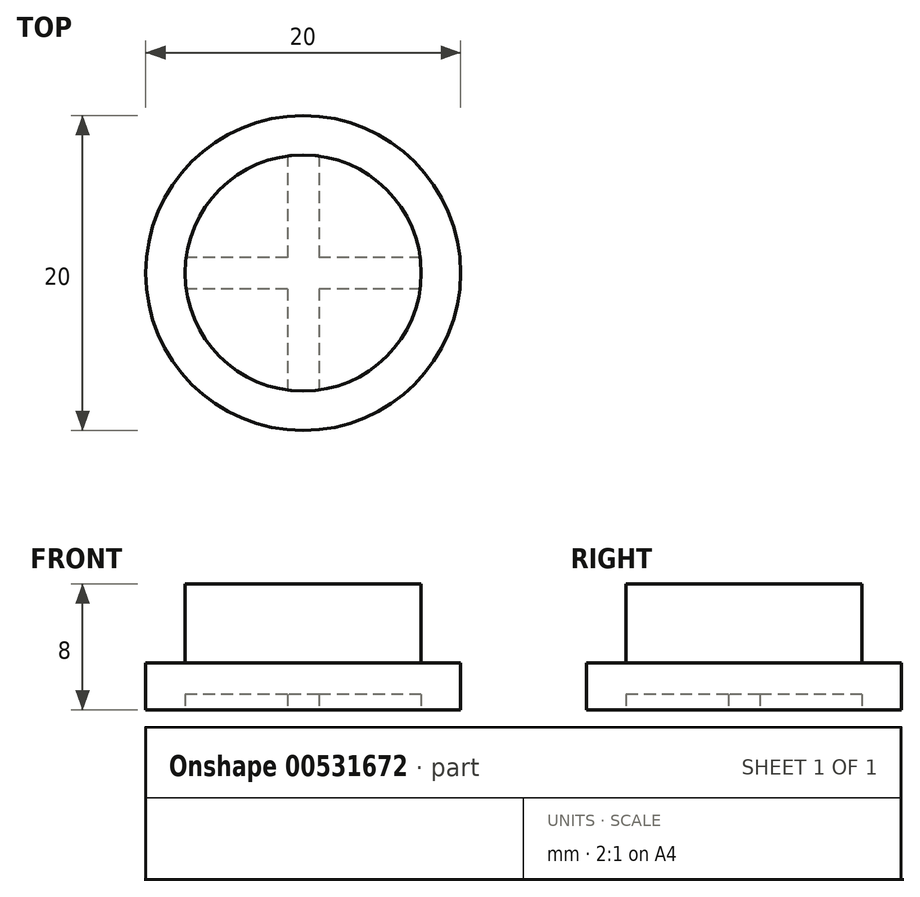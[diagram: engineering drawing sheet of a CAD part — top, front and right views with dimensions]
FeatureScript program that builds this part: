
annotation { "Feature Type Name" : "Feature", "Feature Type Description" : "" }
export const myFeature = defineFeature(function(context is Context, id is Id, definition is map)
    precondition{}
    {
        {
            var Q0;
            Q0=qCreatedBy(makeId("Top.planeOp"),FACE);
            var sketch = newSketch(context, id + "F0", { "sketchPlane" : qUnion([Q0])});
            skCircle(sketch, "E0", {"center": v(0, 0) * mm, "radius": 10 * mm});
            skSolve(sketch);
        }
        {
            var Q0;
            Q0=qSketchRegion(id+"F0",true);
            extrude(context, id + "F1", {"entities" : qUnion([Q0]), "depth" : 3 * mm, "offsetDistance" : 25 * mm});
        }
        {
            var Q0;
            Q0=makeQuery(id+"F1.opExtrude","CAP_FACE",FACE,{"disambiguationData":[OSD([sQuery(id+"F0.wireOp",EDGE,"E0")])],"isStart":false});
            var sketch = newSketch(context, id + "F2", { "sketchPlane" : qUnion([Q0])});
            skCircle(sketch, "E1", {"center": v(0, 0) * mm, "radius": 7.5 * mm});
            skSolve(sketch);
        }
        {
            var Q0;
            Q0=qSketchRegion(id+"F2",true);
            extrude(context, id + "F3", {"entities" : qUnion([Q0]), "operationType" : NewBodyOperationType.ADD, "depth" : 5 * mm, "offsetDistance" : 25 * mm});
        }
        {
            var Q0;
            Q0=makeQuery(id+"F1.opExtrude","CAP_FACE",FACE,{"disambiguationData":[OSD([sQuery(id+"F0.wireOp",EDGE,"E0")])],"isStart":true});
            var sketch = newSketch(context, id + "F4", { "sketchPlane" : qUnion([Q0])});
            skLineSegment(sketch, "E2.bottom", {"start": v(7.5, -1) * mm, "end": v(-7.5, -1) * mm});
            skLineSegment(sketch, "E2.top", {"start": v(7.5, 1) * mm, "end": v(-7.5, 1) * mm});
            skLineSegment(sketch, "E2.left", {"start": v(7.5, -1) * mm, "end": v(7.5, 1) * mm});
            skLineSegment(sketch, "E2.right", {"start": v(-7.5, -1) * mm, "end": v(-7.5, 1) * mm});
            skPoint(sketch, "E2.middle", {"position": v(0, 0) * mm});
            skLineSegment(sketch, "E3.bottom", {"start": v(1, -7.5) * mm, "end": v(-1, -7.5) * mm});
            skLineSegment(sketch, "E3.top", {"start": v(1, 7.5) * mm, "end": v(-1, 7.5) * mm});
            skLineSegment(sketch, "E3.left", {"start": v(1, -7.5) * mm, "end": v(1, 7.5) * mm});
            skLineSegment(sketch, "E3.right", {"start": v(-1, -7.5) * mm, "end": v(-1, 7.5) * mm});
            skSolve(sketch);
        }
        {
            var Q0;
            Q0=qSketchRegion(id+"F4",true);
            extrude(context, id + "F5", {"entities" : qUnion([Q0]), "operationType" : NewBodyOperationType.REMOVE, "oppositeDirection" : true, "depth" : 1 * mm});
        }
    });
